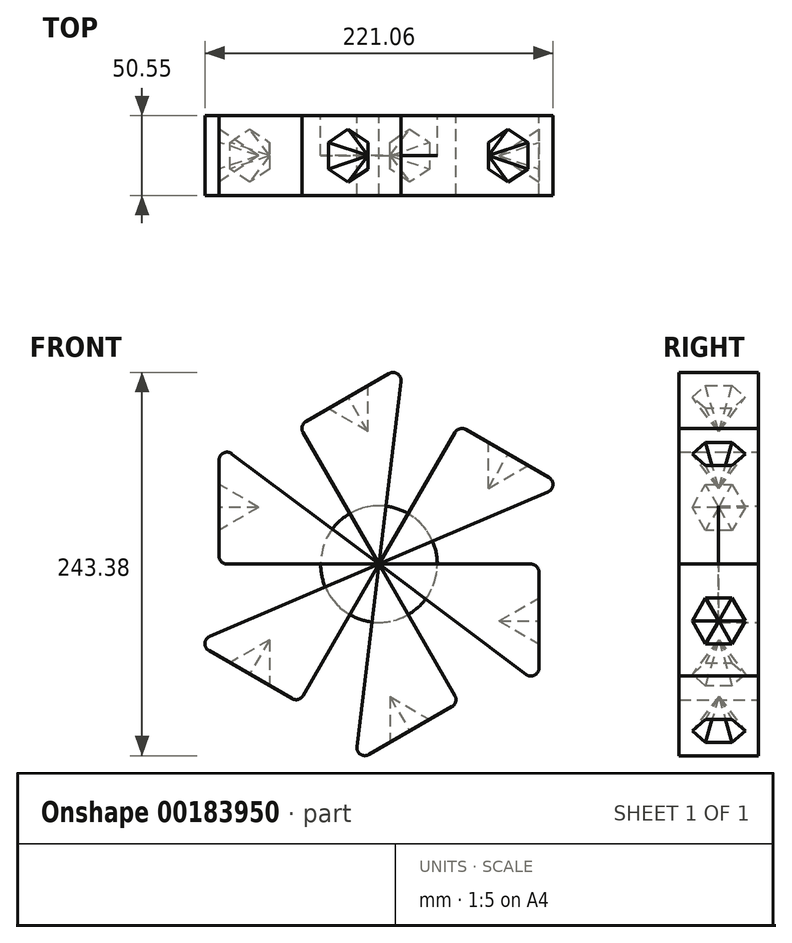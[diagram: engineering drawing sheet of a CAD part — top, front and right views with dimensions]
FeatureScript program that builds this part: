
annotation { "Feature Type Name" : "Feature", "Feature Type Description" : "" }
export const myFeature = defineFeature(function(context is Context, id is Id, definition is map)
    precondition{}
    {
        {
            var Q0;
            Q0=qCreatedBy(makeId("Front.planeOp"),FACE);
            var sketch = newSketch(context, id + "F0", { "sketchPlane" : qUnion([Q0])});
            skLineSegment(sketch, "E0", {"start": v(-45.28, 27.68) * mm, "end": v(56.32, 27.68) * mm});
            skLineSegment(sketch, "E1", {"start": v(56.32, 27.68) * mm, "end": v(56.32, -48.52) * mm});
            skLineSegment(sketch, "E2", {"start": v(56.32, -48.52) * mm, "end": v(-45.28, 27.68) * mm});
            skSolve(sketch);
        }
        {
            var Q0;
            Q0=makeQuery(id+"F0.imprint","IMPRINT",FACE,{"disambiguationData":[TD([[makeQuery(id+"F0.imprint","IMPRINT",EDGE,{"derivedFrom":sQuery(id+"F0.wireOp",EDGE,"E0")}),-1.0]])]});
            extrude(context, id + "F1", {"entities" : qUnion([Q0]), "depth" : 50.55 * mm});
        }
        {
            var Q0;
            Q0=makeQuery(id+"F1.opExtrude","SWEPT_EDGE",EDGE,{"disambiguationData":[OSD([sQuery(id+"F0.wireOp",EDGE,"E1"),sQuery(id+"F0.wireOp",EDGE,"E2")])]});
            var Q1;
            Q1=makeQuery(id+"F1.opExtrude","SWEPT_EDGE",EDGE,{"disambiguationData":[OSD([sQuery(id+"F0.wireOp",EDGE,"E0"),sQuery(id+"F0.wireOp",EDGE,"E1")])]});
            fillet(context, id + "F2", {"entities" : qUnion([Q0, Q1]), "radius" : 5.08 * mm, "tangentPropagation" : true, "allowEdgeOverflow" : false});
        }
        {
            var Q0;
            Q0=makeQuery(id+"F1.opExtrude","SWEPT_FACE",FACE,{"disambiguationData":[OSD([sQuery(id+"F0.wireOp",EDGE,"E1")])]});
            var sketch = newSketch(context, id + "F3", { "sketchPlane" : qUnion([Q0])});
            skCircle(sketch, "E3.cCircle", {"center": v(-25.27, -8.42) * mm, "radius": 14.58 * mm, "construction": true});
            skPoint(sketch, "E3.cCircle.centerSnap0", {"position": v(-25.27, -38.36) * mm});
            skLineSegment(sketch, "E3.0", {"start": v(-33.7, 6.16) * mm, "end": v(-16.85, 6.16) * mm});
            skLineSegment(sketch, "E3.1", {"start": v(-16.85, 6.16) * mm, "end": v(-8.43, -8.42) * mm});
            skLineSegment(sketch, "E3.2", {"start": v(-8.43, -8.42) * mm, "end": v(-16.85, -23) * mm});
            skLineSegment(sketch, "E3.3", {"start": v(-16.85, -23) * mm, "end": v(-33.7, -23) * mm});
            skLineSegment(sketch, "E3.4", {"start": v(-33.7, -23) * mm, "end": v(-42.11, -8.42) * mm});
            skLineSegment(sketch, "E3.5", {"start": v(-42.11, -8.42) * mm, "end": v(-33.7, 6.16) * mm});
            skPoint(sketch, "E3.0.midPoint", {"position": v(-25.27, 6.16) * mm});
            skSolve(sketch);
        }
        {
            var Q0;
            Q0=makeQuery(id+"F3.imprint","IMPRINT",FACE,{"disambiguationData":[TD([[makeQuery(id+"F3.imprint","IMPRINT",EDGE,{"derivedFrom":sQuery(id+"F3.wireOp",EDGE,"E3.0")}),-1.0]])]});
            extrude(context, id + "F4", {"entities" : qUnion([Q0]), "operationType" : NewBodyOperationType.REMOVE, "oppositeDirection" : true, "depth" : 100.33 * mm, "hasDraft" : true, "draftAngle" : 30 * degree, "draftPullDirection" : true});
        }
        {
            var Q0;
            Q0=makeQuery(id+"F1.opExtrude","SWEPT_BODY",BODY,{"disambiguationData":[OSD([sQuery(id+"F0.wireOp",EDGE,"E0"),sQuery(id+"F0.wireOp",EDGE,"E1"),sQuery(id+"F0.wireOp",EDGE,"E2")])]});
            var Q1;
            Q1=makeQuery(id+"F1.opExtrude","SWEPT_EDGE",EDGE,{"disambiguationData":[OSD([sQuery(id+"F0.wireOp",EDGE,"E0"),sQuery(id+"F0.wireOp",EDGE,"E2")])]});
            circularPattern(context, id + "F5", {"entities" : qUnion([Q0]), "axis" : qUnion([Q1]), "angle" : 360 * degree, "instanceCount" : 6, "equalSpace" : true, "computeTransformsWithoutBuiltin" : true});
        }
        {
            var Q0;
            Q0=qCreatedBy(makeId("Front.planeOp"),FACE);
            var sketch = newSketch(context, id + "F6", { "sketchPlane" : qUnion([Q0])});
            skCircle(sketch, "E4", {"center": v(-45.28, 27.68) * mm, "radius": 37.04 * mm});
            skSolve(sketch);
        }
        {
            var Q0;
            Q0=makeQuery(id+"F6.imprint","IMPRINT",FACE,{"disambiguationData":[TD([[makeQuery(id+"F6.imprint","IMPRINT",EDGE,{"derivedFrom":sQuery(id+"F6.wireOp",EDGE,"E4")}),1.0]])]});
            extrude(context, id + "F7", {"entities" : qUnion([Q0]), "depth" : 25.4 * mm});
        }
    });
